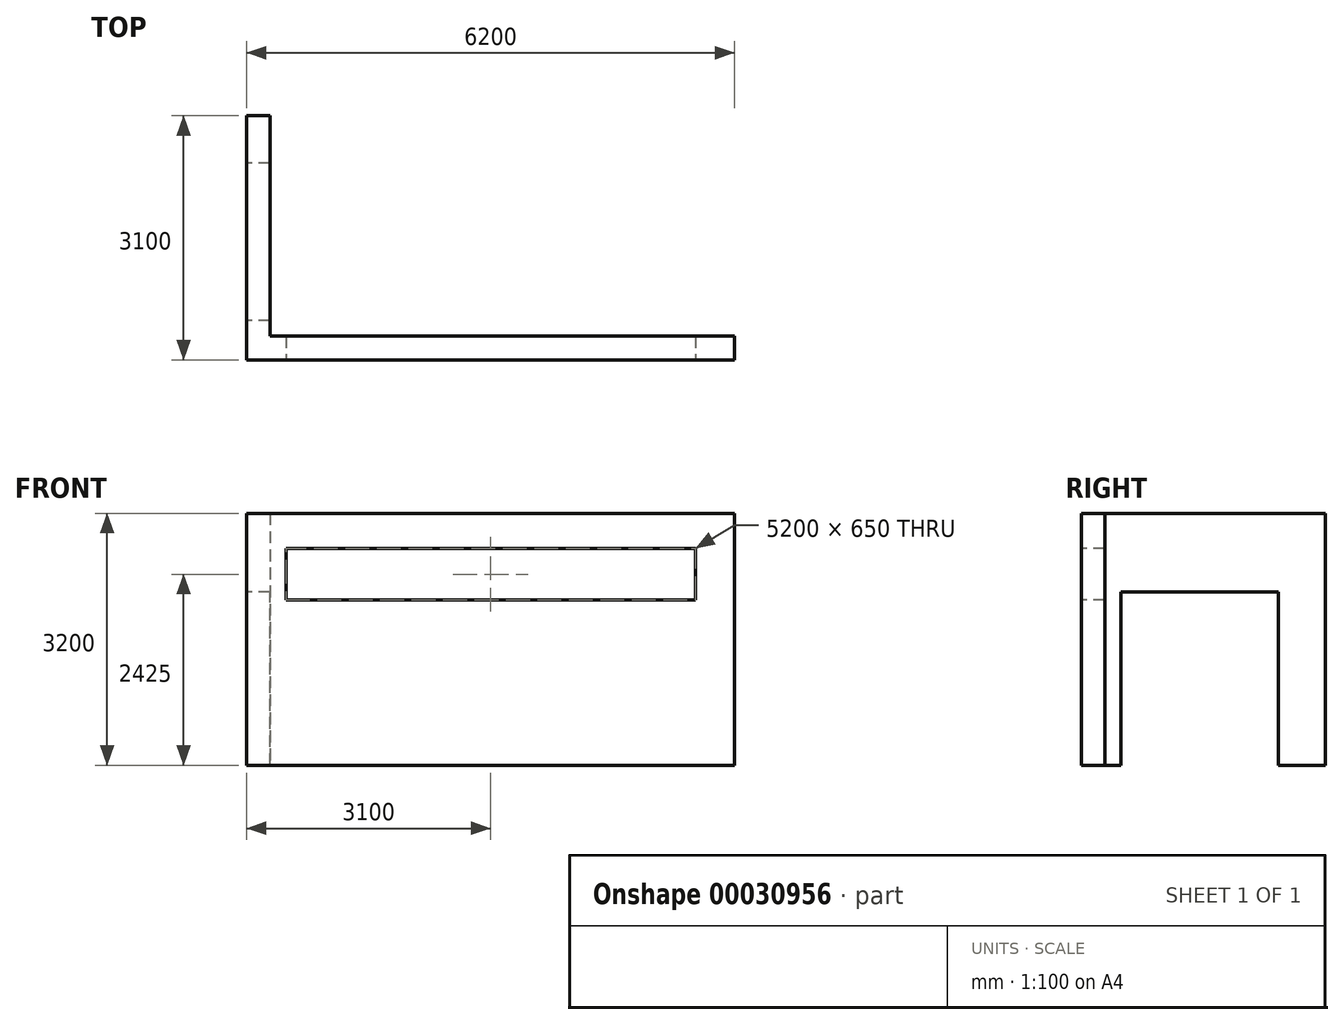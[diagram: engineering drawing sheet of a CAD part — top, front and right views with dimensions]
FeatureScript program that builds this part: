
annotation { "Feature Type Name" : "Feature", "Feature Type Description" : "" }
export const myFeature = defineFeature(function(context is Context, id is Id, definition is map)
    precondition{}
    {
        {
            var Q0;
            Q0=qCreatedBy(makeId("Top.planeOp"),FACE);
            var sketch = newSketch(context, id + "F0", { "sketchPlane" : qUnion([Q0])});
            skLineSegment(sketch, "E0", {"start": v(6200, 0) * mm, "end": v(0, 0) * mm});
            skLineSegment(sketch, "E1", {"start": v(0, 0) * mm, "end": v(0, 3100) * mm});
            skLineSegment(sketch, "E2.0", {"start": v(300, 300) * mm, "end": v(300, 3100) * mm});
            skLineSegment(sketch, "E3.0", {"start": v(6200, 300) * mm, "end": v(300, 300) * mm});
            skLineSegment(sketch, "E4", {"start": v(0, 3100) * mm, "end": v(300, 3100) * mm});
            skLineSegment(sketch, "E5", {"start": v(6200, 0) * mm, "end": v(6200, 300) * mm});
            skSolve(sketch);
        }
        {
            var Q0;
            Q0 = qSketchRegion(id + "F0", true);
            extrude(context, id + "F1", {"entities" : qUnion([Q0]), "depth" : 3200 * mm});
        }
        {
            var Q0;
            Q0=makeQuery(id+"F1.opExtrude","SWEPT_FACE",FACE,{"disambiguationData":[OSD([sQuery(id+"F0.wireOp",EDGE,"E1")])]});
            var sketch = newSketch(context, id + "F2", { "sketchPlane" : qUnion([Q0])});
            skLineSegment(sketch, "E6.bottom", {"start": v(-2500, 0) * mm, "end": v(-500, 0) * mm});
            skLineSegment(sketch, "E6.top", {"start": v(-2500, 2200) * mm, "end": v(-500, 2200) * mm});
            skLineSegment(sketch, "E6.left", {"start": v(-2500, 0) * mm, "end": v(-2500, 2200) * mm});
            skLineSegment(sketch, "E6.right", {"start": v(-500, 0) * mm, "end": v(-500, 2200) * mm});
            skSolve(sketch);
        }
        {
            var Q0;
            Q0 = qSketchRegion(id + "F2", true);
            extrude(context, id + "F3", {"entities" : qUnion([Q0]), "operationType" : NewBodyOperationType.REMOVE, "oppositeDirection" : true, "depth" : 1000 * mm});
        }
        {
            var Q0;
            Q0=makeQuery(id+"F1.opExtrude","SWEPT_FACE",FACE,{"disambiguationData":[OSD([sQuery(id+"F0.wireOp",EDGE,"E0")])]});
            var sketch = newSketch(context, id + "F4", { "sketchPlane" : qUnion([Q0])});
            skLineSegment(sketch, "E7.bottom", {"start": v(500, 2750) * mm, "end": v(5700, 2750) * mm});
            skLineSegment(sketch, "E7.top", {"start": v(500, 2100) * mm, "end": v(5700, 2100) * mm});
            skLineSegment(sketch, "E7.left", {"start": v(500, 2750) * mm, "end": v(500, 2100) * mm});
            skLineSegment(sketch, "E7.right", {"start": v(5700, 2750) * mm, "end": v(5700, 2100) * mm});
            skSolve(sketch);
        }
        {
            var Q0;
            Q0=makeQuery(id+"F4.imprint","IMPRINT",FACE,{"disambiguationData":[TD([[makeQuery(id+"F4.imprint","IMPRINT",EDGE,{"derivedFrom":sQuery(id+"F4.wireOp",EDGE,"E7.bottom")}),-1.0]])]});
            extrude(context, id + "F5", {"entities" : qUnion([Q0]), "operationType" : NewBodyOperationType.REMOVE, "oppositeDirection" : true, "depth" : 1000 * mm});
        }
    });
